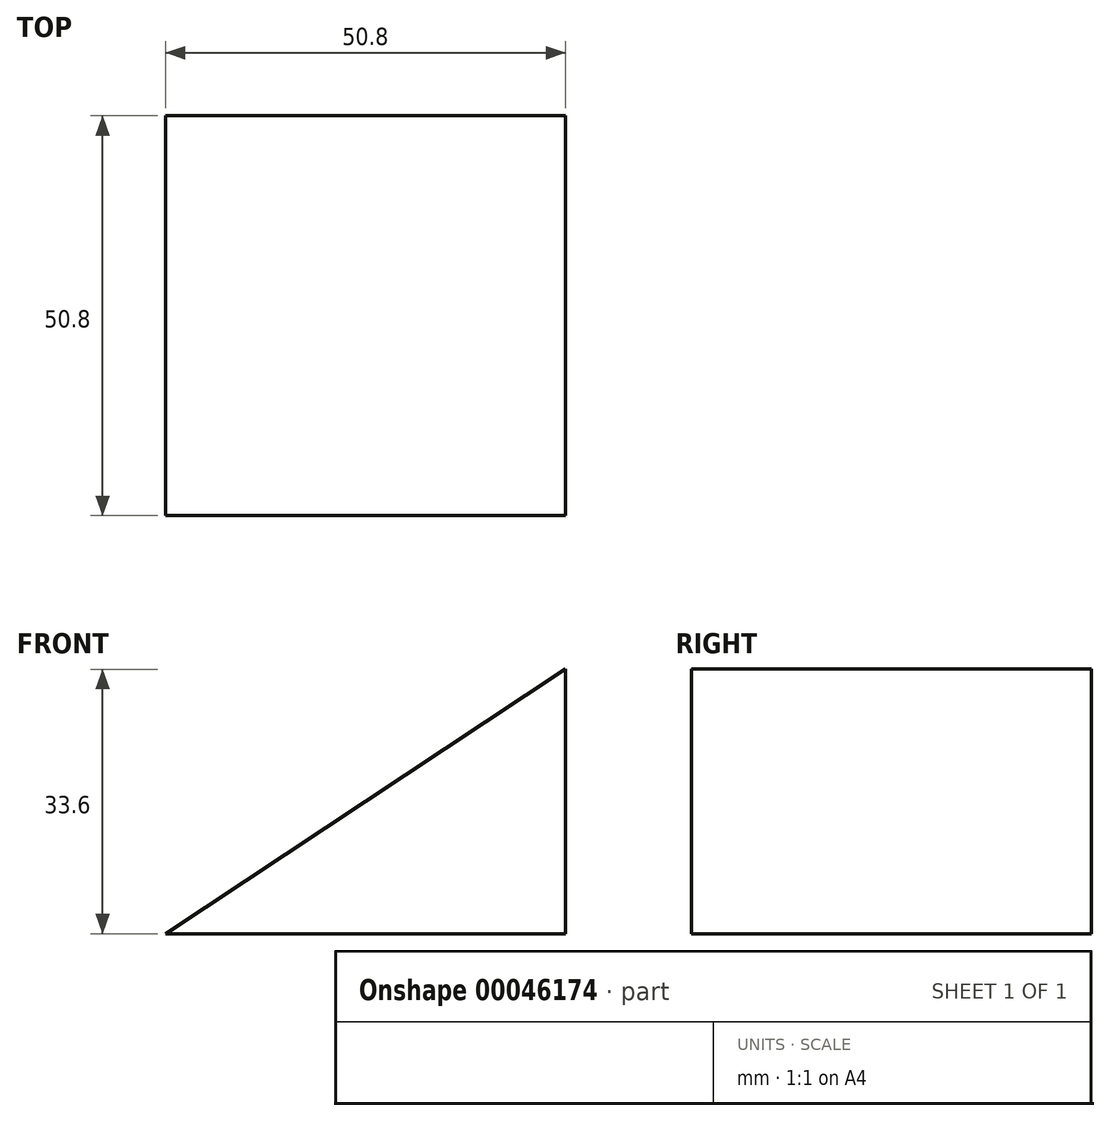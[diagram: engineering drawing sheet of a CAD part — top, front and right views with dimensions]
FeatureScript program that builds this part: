
annotation { "Feature Type Name" : "Feature", "Feature Type Description" : "" }
export const myFeature = defineFeature(function(context is Context, id is Id, definition is map)
    precondition{}
    {
        {
            var Q0;
            Q0=qCreatedBy(makeId("Front.planeOp"),FACE);
            var sketch = newSketch(context, id + "F0", { "sketchPlane" : qUnion([Q0])});
            skLineSegment(sketch, "E0", {"start": v(0, 0) * mm, "end": v(25.4, 0) * mm});
            skLineSegment(sketch, "E1", {"start": v(25.4, 0) * mm, "end": v(25.37, 33.6) * mm});
            skLineSegment(sketch, "E2", {"start": v(25.37, 33.6) * mm, "end": v(-25.4, 0) * mm});
            skLineSegment(sketch, "E3", {"start": v(-25.4, 0) * mm, "end": v(0, 0) * mm});
            skSolve(sketch);
        }
        {
            var Q0;
            Q0=makeQuery(id+"F0.imprint","IMPRINT",FACE,{"disambiguationData":[TD([[makeQuery(id+"F0.imprint","IMPRINT",EDGE,{"derivedFrom":sQuery(id+"F0.wireOp",EDGE,"E0")}),1.0]])]});
            extrude(context, id + "F1", {"entities" : qUnion([Q0]), "depth" : 50.8 * mm});
        }
    });
